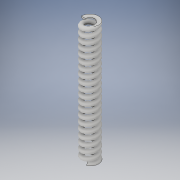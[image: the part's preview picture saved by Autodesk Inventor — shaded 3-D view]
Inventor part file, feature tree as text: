
AUTODESK INVENTOR PART (.ipt)
format: ipt  version: 2018 (Build 220112000, 112)  size: 636,416 bytes
history: native  units: in
note: dims shown in document units (in); Inventor stores cm internally (conversion verified against a paired STEP export)
features: sketch x2, helix x1, extrude x1
ambient origin geometry x8: Origin, YZ Plane, XZ Plane, XY Plane, X Axis, Y Axis, Z Axis, Center Point
bodies: Solid1 (feature_tree)
feature tree (4):
  helix  "Coil1"  [1 undecoded]
  extrude  "Extrusion1"  Depth=0.737in TaperAngle=0.0deg
  sketch  "Sketch1"  dims[d1=0.0531in]
  sketch  "Sketch2"  dims[d2=1.0in d3=0.737in d4=7.874in d5=0.0in d6=90.0deg d7=30.0deg d8=90.0deg d9=30.0deg d10=1.0in d11=0.0in]
note: 1 required parameter value undecoded (feature->parameter linkage not recoverable at this tier; creation-order binding heuristic only, values carry confidence <= 0.55)
